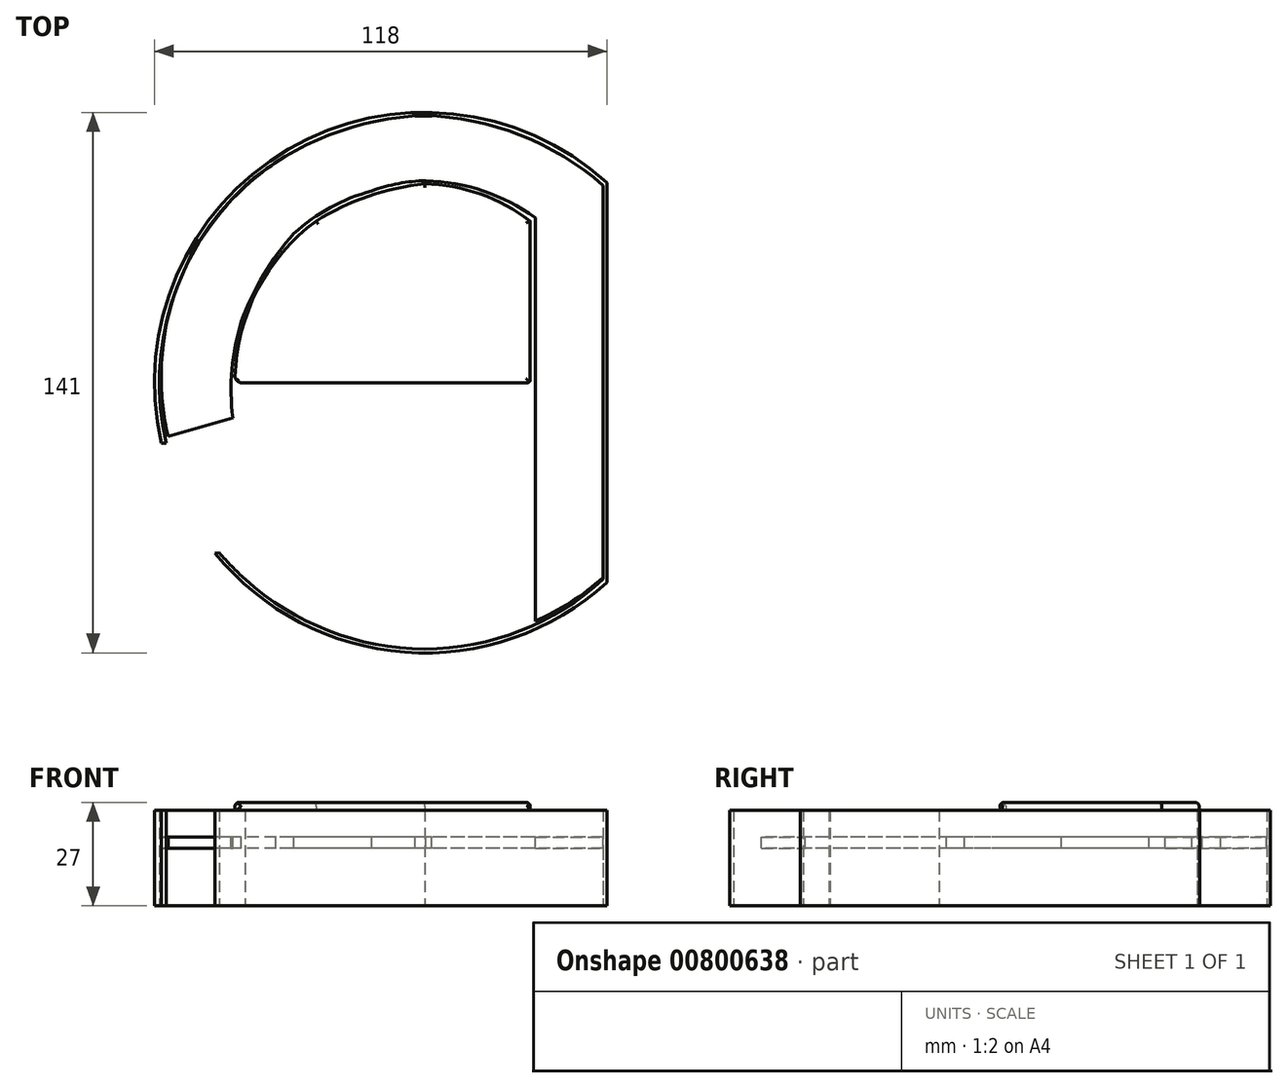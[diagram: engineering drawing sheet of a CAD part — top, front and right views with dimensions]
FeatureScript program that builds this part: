
annotation { "Feature Type Name" : "Feature", "Feature Type Description" : "" }
export const myFeature = defineFeature(function(context is Context, id is Id, definition is map)
    precondition{}
    {
        {
            var Q0;
            Q0=qCreatedBy(makeId("Top.planeOp"),FACE);
            var sketch = newSketch(context, id + "F0", { "sketchPlane" : qUnion([Q0])});
            skArc(sketch, "E0", {"start": v(-54.66, -44.53) * mm, "mid": v(-5.21, -70.3) * mm, "end": v(47.5, -52.1) * mm});
            skLineSegment(sketch, "E1", {"start": v(-70.5, 0) * mm, "end": v(47.5, 0) * mm, "construction": true});
            skLineSegment(sketch, "E2", {"start": v(47.5, 0) * mm, "end": v(47.5, 72.6) * mm, "construction": true});
            skLineSegment(sketch, "E3", {"start": v(47.5, 0) * mm, "end": v(47.5, -75.67) * mm, "construction": true});
            skLineSegment(sketch, "E4", {"start": v(0, -70.5) * mm, "end": v(0, -45.5) * mm, "construction": true});
            skLineSegment(sketch, "E5", {"start": v(0, -45.5) * mm, "end": v(-96.16, -45.5) * mm, "construction": true});
            skLineSegment(sketch, "E6", {"start": v(0, 0) * mm, "end": v(0, -15) * mm, "construction": true});
            skLineSegment(sketch, "E7", {"start": v(0, -15) * mm, "end": v(-100.17, -15) * mm, "construction": true});
            skPoint(sketch, "E8", {"position": v(-68.7, -15.83) * mm});
            skPoint(sketch, "E9", {"position": v(-54.66, -44.53) * mm});
            skPoint(sketch, "E10", {"position": v(-67.42, -15.82) * mm});
            skPoint(sketch, "E11", {"position": v(-53.56, -44.35) * mm});
            skPoint(sketch, "E12", {"position": v(46.5, -51.27) * mm});
            skPoint(sketch, "E13", {"position": v(46.5, 51.45) * mm});
            skPoint(sketch, "E14", {"position": v(0, 69.66) * mm});
            skPoint(sketch, "E15", {"position": v(-46.86, 51.45) * mm});
            skPoint(sketch, "E16", {"position": v(-46.86, -51.27) * mm});
            skArc(sketch, "E17", {"start": v(-46.86, 51.45) * mm, "mid": v(-66.12, 20.56) * mm, "end": v(-67.42, -15.82) * mm});
            skArc(sketch, "E18", {"start": v(0, 69.66) * mm, "mid": v(-25, 64.58) * mm, "end": v(-46.86, 51.45) * mm});
            skArc(sketch, "E19", {"start": v(46.5, 51.45) * mm, "mid": v(24.84, 64.62) * mm, "end": v(0, 69.66) * mm});
            skLineSegment(sketch, "E20", {"start": v(46.5, 51.45) * mm, "end": v(46.5, -51.27) * mm});
            skPoint(sketch, "E21", {"position": v(0, -69.48) * mm});
            skArc(sketch, "E22", {"start": v(0, -69.48) * mm, "mid": v(24.94, -64.7) * mm, "end": v(46.5, -51.27) * mm});
            skArc(sketch, "E23", {"start": v(-46.86, -51.27) * mm, "mid": v(-25.11, -64.7) * mm, "end": v(0, -69.48) * mm});
            skArc(sketch, "E24", {"start": v(-53.56, -44.35) * mm, "mid": v(-50.33, -47.93) * mm, "end": v(-46.86, -51.27) * mm});
            skLineSegment(sketch, "E25", {"start": v(-53.56, -44.35) * mm, "end": v(-54.66, -44.53) * mm});
            skLineSegment(sketch, "E26", {"start": v(-67.42, -15.82) * mm, "end": v(-68.7, -15.83) * mm});
            skPoint(sketch, "E27", {"position": v(47.5, -52.1) * mm});
            skPoint(sketch, "E28", {"position": v(47.5, 52.1) * mm});
            skLineSegment(sketch, "E29", {"start": v(47.5, 52.1) * mm, "end": v(47.5, -52.1) * mm});
            skArc(sketch, "E30.trimOffspring", {"start": v(47.5, 52.1) * mm, "mid": v(-35.58, 60.86) * mm, "end": v(-68.7, -15.83) * mm});
            skSolve(sketch);
        }
        {
            var Q0;
            Q0 = qSketchRegion(id + "F0", true);
            extrude(context, id + "F1", {"entities" : qUnion([Q0]), "depth" : 25 * mm, "offsetDistance" : 25 * mm});
        }
        {
            var Q0;
            Q0=qCreatedBy(makeId("Top.planeOp"),FACE);
            cPlane(context, id + "F2", {"entities" : qUnion([Q0]), "cplaneType" : CPlaneType.OFFSET, "offset" : 18 * mm, "width" : 150 * mm, "height" : 150 * mm});
        }
        {
            var Q0;
            Q0=qCreatedBy(id+"F2.planeOp",FACE);
            var sketch = newSketch(context, id + "F3", { "sketchPlane" : qUnion([Q0])});
            skPoint(sketch, "E31", {"position": v(-50.05, -9.22) * mm});
            skLineSegment(sketch, "E32", {"start": v(0.3, 70.67) * mm, "end": v(0.3, 52.67) * mm, "construction": true});
            skPoint(sketch, "E33", {"position": v(0.3, 52.67) * mm});
            skPoint(sketch, "E34", {"position": v(28.8, 43.05) * mm});
            skPoint(sketch, "E35", {"position": v(-34.1, 38.92) * mm});
            skPoint(sketch, "E36", {"position": v(-47.82, 16.01) * mm});
            skPoint(sketch, "E37", {"position": v(28.8, 0.47) * mm});
            skPoint(sketch, "E38", {"position": v(46.67, 0.47) * mm});
            skPoint(sketch, "E39", {"position": v(28.8, 22.23) * mm});
            skPoint(sketch, "E40", {"position": v(28.8, -29.46) * mm});
            skPoint(sketch, "E41", {"position": v(28.8, -62.2) * mm});
            skPoint(sketch, "E42", {"position": v(28.8, -46.62) * mm});
            skPoint(sketch, "E43", {"position": v(-13.83, 50) * mm});
            skArc(sketch, "E44", {"start": v(-47.82, 16.01) * mm, "mid": v(-50.26, 3.51) * mm, "end": v(-50.05, -9.22) * mm});
            skArc(sketch, "E45", {"start": v(-34.1, 38.92) * mm, "mid": v(-42.02, 28.1) * mm, "end": v(-47.82, 16.01) * mm});
            skArc(sketch, "E46", {"start": v(-13.83, 50) * mm, "mid": v(-24.63, 45.67) * mm, "end": v(-34.1, 38.92) * mm});
            skArc(sketch, "E47", {"start": v(0.3, 52.67) * mm, "mid": v(-6.88, 51.96) * mm, "end": v(-13.83, 50) * mm});
            skArc(sketch, "E48", {"start": v(28.8, 43.05) * mm, "mid": v(15.27, 50) * mm, "end": v(0.3, 52.67) * mm});
            skLineSegment(sketch, "E49", {"start": v(28.8, 43.05) * mm, "end": v(28.8, -62.2) * mm});
            skLineSegment(sketch, "E50", {"start": v(-50.05, -9.22) * mm, "end": v(-66.93, -14) * mm});
            skPoint(sketch, "E51", {"position": v(-37.71, 58.26) * mm});
            skPoint(sketch, "E52", {"position": v(-18.38, 67.01) * mm});
            skPoint(sketch, "E53", {"position": v(22.38, 65.97) * mm});
            skPoint(sketch, "E54", {"position": v(-0.2, 70.06) * mm});
            skPoint(sketch, "E55", {"position": v(9.88, 69.11) * mm});
            skPoint(sketch, "E56", {"position": v(46.7, 52) * mm});
            skPoint(sketch, "E57", {"position": v(33.86, 60.88) * mm});
            skPoint(sketch, "E58", {"position": v(-55.8, 41.07) * mm});
            skPoint(sketch, "E59", {"position": v(-68.74, 2.23) * mm});
            skArc(sketch, "E60", {"start": v(-68.74, 2.23) * mm, "mid": v(-68.3, -5.94) * mm, "end": v(-66.93, -14) * mm});
            skArc(sketch, "E61", {"start": v(-55.8, 41.07) * mm, "mid": v(-65.34, 22.67) * mm, "end": v(-68.74, 2.23) * mm});
            skArc(sketch, "E62", {"start": v(46.7, 52) * mm, "mid": v(-6.96, 69.2) * mm, "end": v(-55.8, 41.07) * mm});
            skLineSegment(sketch, "E63", {"start": v(46.7, 52) * mm, "end": v(46.7, -50.64) * mm});
            skArc(sketch, "E64", {"start": v(28.8, -62.2) * mm, "mid": v(38.22, -57.14) * mm, "end": v(46.7, -50.64) * mm});
            skSolve(sketch);
        }
        {
            var Q0;
            Q0 = qSketchRegion(id + "F3", true);
            extrude(context, id + "F4", {"entities" : qUnion([Q0]), "operationType" : NewBodyOperationType.ADD, "oppositeDirection" : true, "depth" : 3 * mm, "offsetDistance" : 25 * mm});
        }
        {
            var Q0;
            Q0=qCreatedBy(makeId("Top.planeOp"),FACE);
            cPlane(context, id + "F5", {"entities" : qUnion([Q0]), "cplaneType" : CPlaneType.OFFSET, "offset" : 25 * mm, "width" : 150 * mm, "height" : 150 * mm});
        }
        {
            var Q0;
            Q0=qCreatedBy(id+"F5.planeOp",FACE);
            var sketch = newSketch(context, id + "F6", { "sketchPlane" : qUnion([Q0])});
            skArc(sketch, "E65", {"start": v(-28.35, 42.16) * mm, "mid": v(-43.6, 24.28) * mm, "end": v(-49.47, 1.53) * mm});
            skArc(sketch, "E66", {"start": v(0, 51.91) * mm, "mid": v(-14.72, 48.62) * mm, "end": v(-28.35, 42.16) * mm});
            skArc(sketch, "E67", {"start": v(27.48, 42.16) * mm, "mid": v(14.5, 49.2) * mm, "end": v(0, 51.91) * mm});
            skLineSegment(sketch, "E68", {"start": v(27.48, 42.16) * mm, "end": v(27.48, 0.6) * mm});
            skLineSegment(sketch, "E69", {"start": v(26.83, 0) * mm, "end": v(-47.95, 0) * mm});
            skArc(sketch, "E70", {"start": v(-49.47, 1.53) * mm, "mid": v(-48.97, 0.5) * mm, "end": v(-47.95, 0) * mm});
            skPoint(sketch, "E71.orphan", {"position": v(-49.48, 0) * mm});
            skArc(sketch, "E72", {"start": v(26.83, 0) * mm, "mid": v(27.24, 0.21) * mm, "end": v(27.48, 0.6) * mm});
            skPoint(sketch, "E73.orphan", {"position": v(27.48, 0) * mm});
            skSolve(sketch);
        }
        {
            var Q0;
            Q0 = qSketchRegion(id + "F6", true);
            extrude(context, id + "F7", {"entities" : qUnion([Q0]), "depth" : 2 * mm, "offsetDistance" : 25 * mm});
        }
        {
            var Q0;
            Q0=makeQuery(id+"F7.opExtrude","CAP_EDGE",EDGE,{"disambiguationData":[OSD([sQuery(id+"F6.wireOp",EDGE,"E65")])],"isStart":false});
            var Q1;
            Q1=makeQuery(id+"F7.opExtrude","CAP_EDGE",EDGE,{"disambiguationData":[OSD([sQuery(id+"F6.wireOp",EDGE,"E67")])],"isStart":false});
            var Q2;
            Q2=makeQuery(id+"F7.opExtrude","CAP_EDGE",EDGE,{"disambiguationData":[OSD([sQuery(id+"F6.wireOp",EDGE,"E68")])],"isStart":false});
            var Q3;
            Q3=makeQuery(id+"F7.opExtrude","CAP_EDGE",EDGE,{"disambiguationData":[OSD([sQuery(id+"F6.wireOp",EDGE,"E69")])],"isStart":false});
            var Q4;
            Q4=makeQuery(id+"F7.opExtrude","CAP_EDGE",EDGE,{"disambiguationData":[OSD([sQuery(id+"F6.wireOp",EDGE,"E69")])],"isStart":true});
            fillet(context, id + "F8", {"entities" : qUnion([Q0, Q1, Q2, Q3, Q4]), "radius" : 1 * mm, "tangentPropagation" : true, "allowEdgeOverflow" : false});
        }
    });
